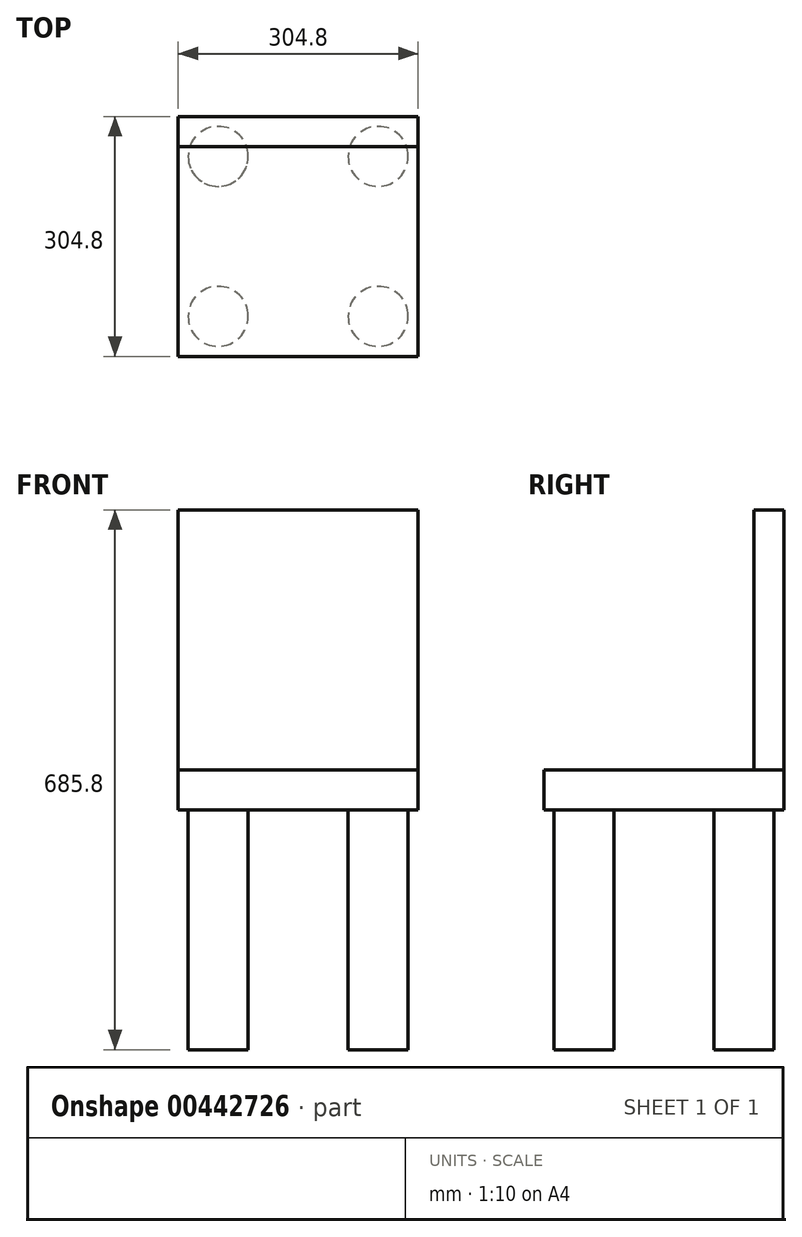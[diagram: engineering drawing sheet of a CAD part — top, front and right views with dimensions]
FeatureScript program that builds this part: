
annotation { "Feature Type Name" : "Feature", "Feature Type Description" : "" }
export const myFeature = defineFeature(function(context is Context, id is Id, definition is map)
    precondition{}
    {
        {
            var Q0;
            Q0=qCreatedBy(makeId("Top.planeOp"),FACE);
            var sketch = newSketch(context, id + "F0", { "sketchPlane" : qUnion([Q0])});
            skLineSegment(sketch, "E0.bottom", {"start": v(152.4, 152.4) * mm, "end": v(-152.4, 152.4) * mm});
            skLineSegment(sketch, "E0.top", {"start": v(152.4, -152.4) * mm, "end": v(-152.4, -152.4) * mm});
            skLineSegment(sketch, "E0.left", {"start": v(152.4, 152.4) * mm, "end": v(152.4, -152.4) * mm});
            skLineSegment(sketch, "E0.right", {"start": v(-152.4, 152.4) * mm, "end": v(-152.4, -152.4) * mm});
            skPoint(sketch, "E0.middle", {"position": v(0, 0) * mm});
            skSolve(sketch);
        }
        {
            var Q0;
            Q0=makeQuery(id+"F0.imprint","IMPRINT",FACE,{"disambiguationData":[TD([[makeQuery(id+"F0.imprint","IMPRINT",EDGE,{"derivedFrom":sQuery(id+"F0.wireOp",EDGE,"E0.bottom")}),1.0]])]});
            extrude(context, id + "F1", {"entities" : qUnion([Q0]), "depth" : 50.8 * mm});
        }
        {
            var Q0;
            Q0=makeQuery(id+"F1.opExtrude","CAP_FACE",FACE,{"disambiguationData":[OSD([sQuery(id+"F0.wireOp",EDGE,"E0.bottom"),sQuery(id+"F0.wireOp",EDGE,"E0.top"),sQuery(id+"F0.wireOp",EDGE,"E0.left"),sQuery(id+"F0.wireOp",EDGE,"E0.right")])],"isStart":true});
            var sketch = newSketch(context, id + "F2", { "sketchPlane" : qUnion([Q0])});
            skCircle(sketch, "E1", {"center": v(-101.6, 101.6) * mm, "radius": 38.1 * mm});
            skSolve(sketch);
        }
        {
            var Q0;
            Q0=makeQuery(id+"F2.imprint","IMPRINT",FACE,{"disambiguationData":[TD([[makeQuery(id+"F2.imprint","IMPRINT",EDGE,{"derivedFrom":sQuery(id+"F2.wireOp",EDGE,"E1")}),1.0]])]});
            extrude(context, id + "F3", {"entities" : qUnion([Q0]), "depth" : 304.8 * mm});
        }
        {
            var Q0;
            Q0=makeQuery(id+"F3.opExtrude","SWEPT_BODY",BODY,{"disambiguationData":[OSD([sQuery(id+"F2.wireOp",EDGE,"E1")])]});
            var Q1;
            Q1=qCreatedBy(makeId("Front.planeOp"),FACE);
            mirror(context, id + "F4", {"operationType" : NewBodyOperationType.ADD, "entities" : qUnion([Q0]), "mirrorPlane" : qUnion([Q1])});
        }
        {
            var Q0;
            Q0=makeQuery(id+"F1.opExtrude","SWEPT_BODY",BODY,{"disambiguationData":[OSD([sQuery(id+"F0.wireOp",EDGE,"E0.bottom"),sQuery(id+"F0.wireOp",EDGE,"E0.top"),sQuery(id+"F0.wireOp",EDGE,"E0.left"),sQuery(id+"F0.wireOp",EDGE,"E0.right")])]});
            var Q1;
            Q1=qCreatedBy(makeId("Right.planeOp"),FACE);
            mirror(context, id + "F5", {"operationType" : NewBodyOperationType.ADD, "entities" : qUnion([Q0]), "mirrorPlane" : qUnion([Q1])});
        }
        {
            var Q0;
            Q0=makeQuery(id+"F1.opExtrude","SWEPT_FACE",FACE,{"disambiguationData":[OSD([sQuery(id+"F0.wireOp",EDGE,"E0.bottom")])]});
            var sketch = newSketch(context, id + "F6", { "sketchPlane" : qUnion([Q0])});
            skLineSegment(sketch, "E2.bottom", {"start": v(152.4, 0) * mm, "end": v(-152.4, 0) * mm});
            skLineSegment(sketch, "E2.top", {"start": v(152.4, 381) * mm, "end": v(-152.4, 381) * mm});
            skLineSegment(sketch, "E2.left", {"start": v(152.4, 0) * mm, "end": v(152.4, 381) * mm});
            skLineSegment(sketch, "E2.right", {"start": v(-152.4, 0) * mm, "end": v(-152.4, 381) * mm});
            skSolve(sketch);
        }
        {
            var Q0;
            {var subQ0=sQuery(id+"F6.wireOp",EDGE,"E2.top");Q0=makeQuery(id+"F6.imprint","IMPRINT",FACE,{"disambiguationData":[TD([[makeQuery(id+"F6.imprint","IMPRINT",EDGE,{"derivedFrom":subQ0}),1.0]])]});}
            extrude(context, id + "F7", {"entities" : qUnion([Q0]), "depth" : -38.1 * mm});
        }
    });
